# Revit family: Toilet-Elongated-American_Standard-Retrospect_Champion_PRO-212CA_Series
name_source: partatom
category: Plumbing Fixtures
revit_build: Autodesk Revit 2014 (Build: 20130308_1515(x64)
units: mm (PartAtom-declared; Revit-internal decimal feet)

## types (2) — shared parameters
ADA Compliant = Yes
Assembly Code = D2010110
Bowl Shape = Elongated
CW Connection = Yes
CWFU = 5
Cold Water Connection Diameter = 1/2"
Cold Water Connection Height = 10"
Cold Water Connection Radius = 1/4"
Cold Water Connection Width = 6"
Default Elevation = 0"
Description = Retrospect Champion PRO Elongated 1.28 gpf Toilet
Flush Rate = 1.28 gpf (4.8 Lpf)
HW Connection = No
Height = 30"
Installation Type = Floor Mounted
Length = 30 1/4"
Manufacturer = American Standard
Price = Prices may vary. Please consult Manufacturer Representative for most up-to-date price list.
Product Documentation Link = https://www.americanstandard-us.com
Product Page URL = https://www.americanstandard-us.com
Revised Date = 01/14/2019
URL = http://www.americanstandard-us.com
Vent Connection = No
WFU = 5
Warranty Information = 10 Year Warranty
Waste Connection = Yes
Waste Connection Diameter = 2 3/8"
Waste Connection Radius = 1 3/16"
Width = 19 3/4"
zero-valued in all types: HWFU

## per-type parameters (varying)
| type | Finish | Material |
| 212CA.104.020 | Vitreous China-American Standard-020-White | Vitreous China-American Standard-020-White |
| 212CA.104.222 | Vitreous China-American Standard-222-Linen | Vitreous China-American Standard-222-Linen |

note: column(s) folded — value = type name in every type: Model

## geometry (parser evidence)
native form markers: Sweep x2
no freeform markers — native parametric forms only
